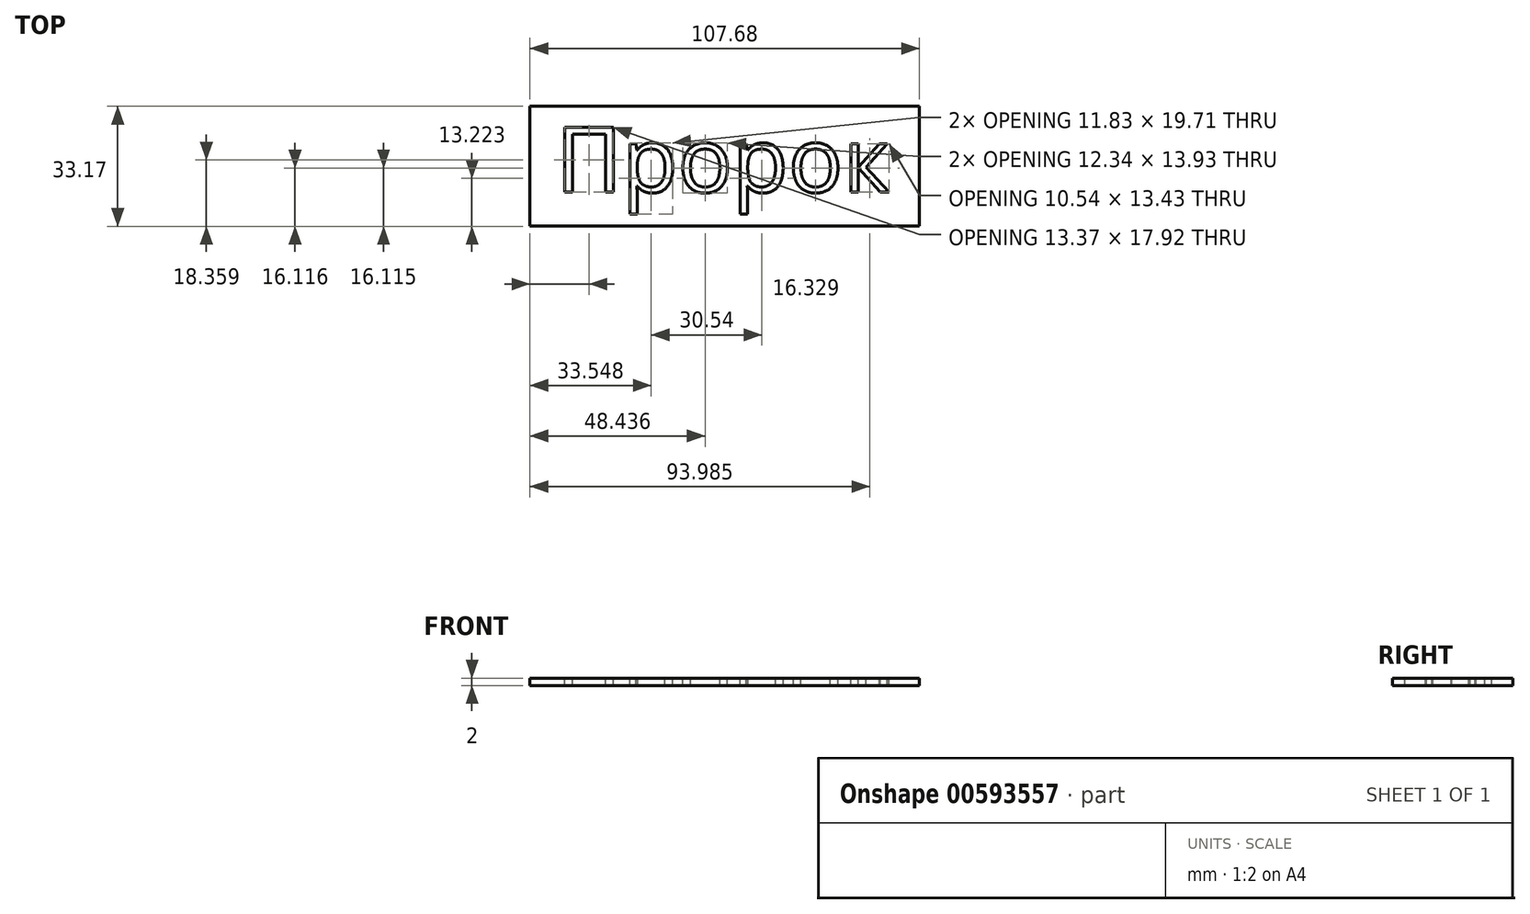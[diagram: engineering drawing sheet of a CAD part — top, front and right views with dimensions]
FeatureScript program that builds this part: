
annotation { "Feature Type Name" : "Feature", "Feature Type Description" : "" }
export const myFeature = defineFeature(function(context is Context, id is Id, definition is map)
    precondition{}
    {
        {
            var Q0;
            Q0=qCreatedBy(makeId("Top.planeOp"),FACE);
            var sketch = newSketch(context, id + "F0", { "sketchPlane" : qUnion([Q0])});
            skLineSegment(sketch, "E0.bottom", {"start": v(-45.42, 45.17) * mm, "end": v(62.26, 45.17) * mm});
            skLineSegment(sketch, "E0.top", {"start": v(-45.42, 12) * mm, "end": v(62.26, 12) * mm});
            skLineSegment(sketch, "E0.left", {"start": v(-45.42, 45.17) * mm, "end": v(-45.42, 12) * mm});
            skLineSegment(sketch, "E0.right", {"start": v(62.26, 45.17) * mm, "end": v(62.26, 12) * mm});
            skSolve(sketch);
        }
        {
            var Q0;
            Q0 = qSketchRegion(id + "F0", true);
            extrude(context, id + "F1", {"entities" : qUnion([Q0]), "depth" : 2 * mm, "offsetDistance" : 25 * mm});
        }
        {
            var Q0;
            Q0=makeQuery(id+"F1.opExtrude","CAP_FACE",FACE,{"disambiguationData":[OSD([sQuery(id+"F0.wireOp",EDGE,"E0.bottom"),sQuery(id+"F0.wireOp",EDGE,"E0.top"),sQuery(id+"F0.wireOp",EDGE,"E0.left"),sQuery(id+"F0.wireOp",EDGE,"E0.right")])],"isStart":false});
            var sketch = newSketch(context, id + "F2", { "sketchPlane" : qUnion([Q0])});
            skText(sketch, "E1", { "text": "Пророк", "fontName": "OpenSans-Regular.ttf"});
            const initialGuessF2  = {"E1": [-0.03824, 0.0214, 1, 0, 0.01807]};
            skSetInitialGuess(sketch, initialGuessF2);
            skSolve(sketch);
        }
        {
            var Q0;
            Q0 = qSketchRegion(id + "F2", true);
            extrude(context, id + "F3", {"entities" : qUnion([Q0]), "operationType" : NewBodyOperationType.REMOVE, "oppositeDirection" : true, "depth" : 25 * mm, "offsetDistance" : 25 * mm});
        }
    });
